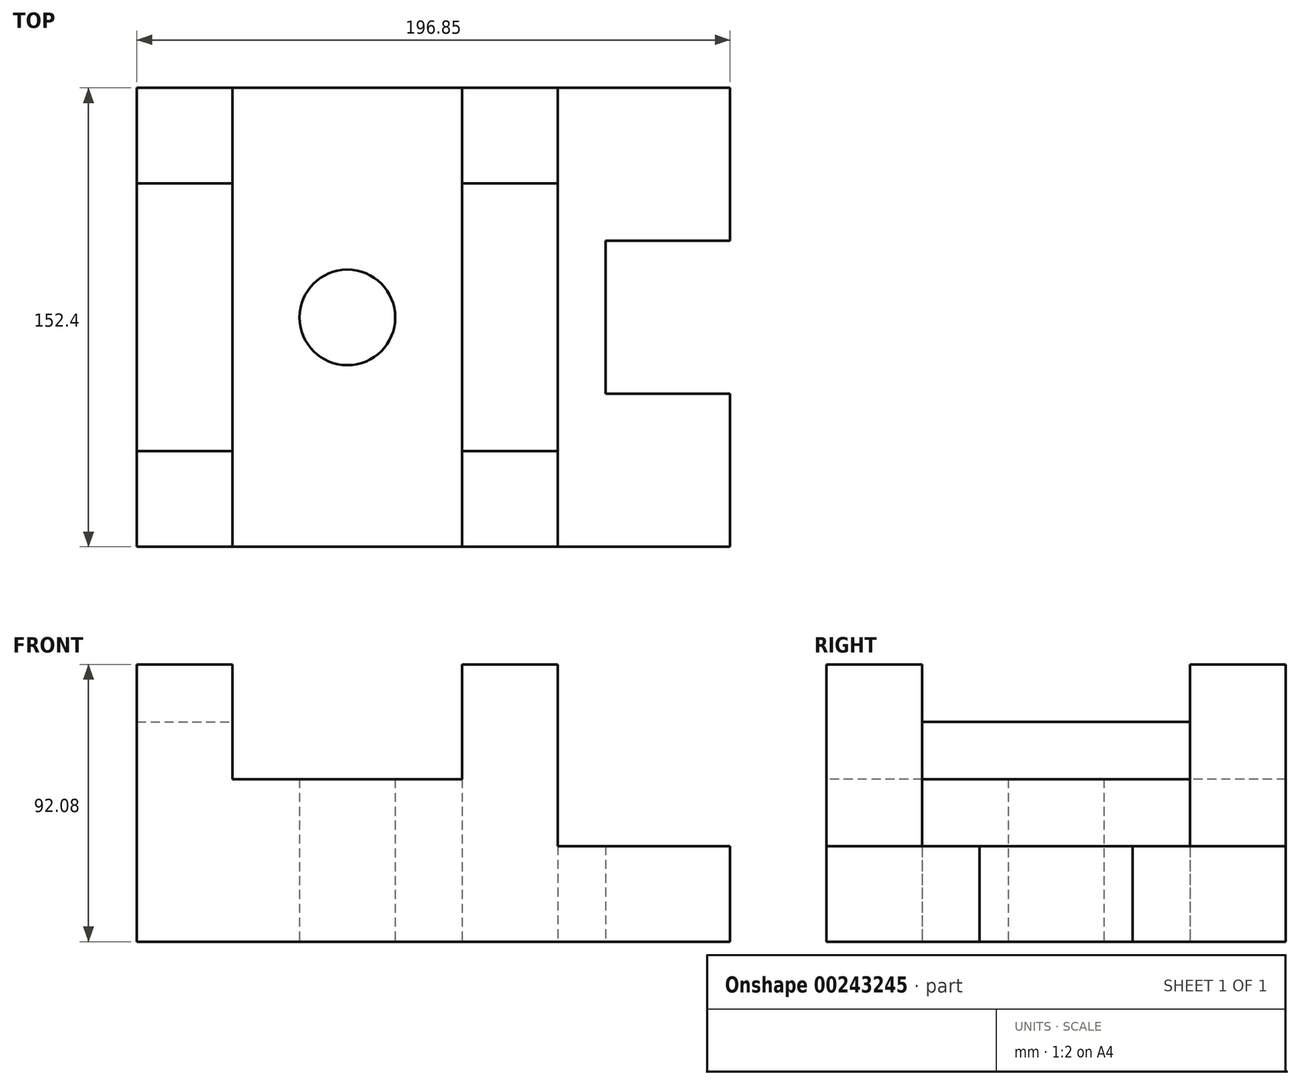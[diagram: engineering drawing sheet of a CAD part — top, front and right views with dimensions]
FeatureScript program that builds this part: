
annotation { "Feature Type Name" : "Feature", "Feature Type Description" : "" }
export const myFeature = defineFeature(function(context is Context, id is Id, definition is map)
    precondition{}
    {
        {
            var Q0;
            Q0=qCreatedBy(makeId("Top.planeOp"),FACE);
            var sketch = newSketch(context, id + "F0", { "sketchPlane" : qUnion([Q0])});
            skLineSegment(sketch, "E0.left", {"start": v(-114.8, 83.68) * mm, "end": v(-114.8, -68.72) * mm});
            skLineSegment(sketch, "E1.bottom", {"start": v(-114.8, 83.68) * mm, "end": v(-57.65, 83.68) * mm});
            skLineSegment(sketch, "E1.top", {"start": v(-114.8, -68.72) * mm, "end": v(-57.65, -68.72) * mm});
            skLineSegment(sketch, "E1.right", {"start": v(-57.65, 83.68) * mm, "end": v(-57.65, -68.72) * mm});
            skLineSegment(sketch, "E2.bottom", {"start": v(-57.65, 83.68) * mm, "end": v(-25.9, 83.68) * mm});
            skLineSegment(sketch, "E2.top", {"start": v(-57.65, -68.72) * mm, "end": v(-25.9, -68.72) * mm});
            skLineSegment(sketch, "E2.right", {"start": v(-25.9, 83.68) * mm, "end": v(-25.9, -68.72) * mm});
            skLineSegment(sketch, "E3.MirrorCS", {"start": v(-114.8, -68.72) * mm, "end": v(-114.8, 83.68) * mm});
            skLineSegment(sketch, "E4.MirrorCS", {"start": v(-57.65, -68.72) * mm, "end": v(-57.65, 83.68) * mm});
            skLineSegment(sketch, "E5.MirrorCS", {"start": v(-25.9, -68.72) * mm, "end": v(-25.9, 83.68) * mm});
            skPoint(sketch, "E6.endSnap0", {"position": v(50.3, -68.72) * mm});
            skLineSegment(sketch, "E7.MirrorCS", {"start": v(-57.65, -68.72) * mm, "end": v(-57.65, -36.97) * mm});
            skLineSegment(sketch, "E8.MirrorCS", {"start": v(-114.8, -17.92) * mm, "end": v(-114.8, 32.88) * mm});
            skLineSegment(sketch, "E9.MirrorCS", {"start": v(-114.8, -68.72) * mm, "end": v(-114.8, -17.92) * mm});
            skLineSegment(sketch, "E10.MirrorCS", {"start": v(-57.65, 83.68) * mm, "end": v(-57.65, 51.93) * mm});
            skLineSegment(sketch, "E11.MirrorCS", {"start": v(-114.8, 83.68) * mm, "end": v(-114.8, 32.88) * mm});
            skLineSegment(sketch, "E12.MirrorCS", {"start": v(-114.8, 32.88) * mm, "end": v(-73.52, 32.88) * mm});
            skLineSegment(sketch, "E13.MirrorCS", {"start": v(-114.8, 32.88) * mm, "end": v(-114.8, -17.92) * mm});
            skLineSegment(sketch, "E14.MirrorCS", {"start": v(-114.8, -17.92) * mm, "end": v(-73.52, -17.92) * mm});
            skLineSegment(sketch, "E15.MirrorCS", {"start": v(-73.52, -17.92) * mm, "end": v(-73.52, 32.88) * mm});
            skLineSegment(sketch, "E16.MirrorCS", {"start": v(-57.65, -36.97) * mm, "end": v(-25.9, -36.97) * mm});
            skLineSegment(sketch, "E17.MirrorCS", {"start": v(-25.9, 83.68) * mm, "end": v(-25.9, 51.93) * mm});
            skLineSegment(sketch, "E18.MirrorCS", {"start": v(-73.52, 32.88) * mm, "end": v(-73.52, -17.92) * mm});
            skLineSegment(sketch, "E19.MirrorCS", {"start": v(-57.65, 51.93) * mm, "end": v(-25.9, 51.93) * mm});
            skPoint(sketch, "E20.MirrorP", {"position": v(3.96, -68.72) * mm});
            skLineSegment(sketch, "E21.MirrorCS", {"start": v(-25.9, -68.72) * mm, "end": v(-25.9, -36.97) * mm});
            skLineSegment(sketch, "E22.bottom", {"start": v(-25.9, 83.68) * mm, "end": v(50.3, 83.68) * mm});
            skLineSegment(sketch, "E22.top", {"start": v(-25.9, -68.72) * mm, "end": v(50.3, -68.72) * mm});
            skLineSegment(sketch, "E22.right", {"start": v(50.3, 83.68) * mm, "end": v(50.3, -68.72) * mm});
            skPoint(sketch, "E23.endSnap0", {"position": v(50.3, 7.48) * mm});
            skLineSegment(sketch, "E24.bottom", {"start": v(50.3, 83.68) * mm, "end": v(82.05, 83.68) * mm});
            skLineSegment(sketch, "E24.top", {"start": v(50.3, 51.93) * mm, "end": v(82.05, 51.93) * mm});
            skLineSegment(sketch, "E24.left", {"start": v(50.3, 83.68) * mm, "end": v(50.3, 51.93) * mm});
            skLineSegment(sketch, "E24.right", {"start": v(82.05, 83.68) * mm, "end": v(82.05, 51.93) * mm});
            skLineSegment(sketch, "E25.bottom", {"start": v(50.3, -68.72) * mm, "end": v(82.05, -68.72) * mm});
            skLineSegment(sketch, "E25.top", {"start": v(50.3, -36.97) * mm, "end": v(82.05, -36.97) * mm});
            skLineSegment(sketch, "E25.left", {"start": v(50.3, -68.72) * mm, "end": v(50.3, -36.97) * mm});
            skLineSegment(sketch, "E25.right", {"start": v(82.05, -68.72) * mm, "end": v(82.05, -36.97) * mm});
            skLineSegment(sketch, "E26.bottom", {"start": v(82.05, 51.93) * mm, "end": v(50.3, 51.93) * mm});
            skLineSegment(sketch, "E26.top", {"start": v(82.05, -36.97) * mm, "end": v(50.3, -36.97) * mm});
            skLineSegment(sketch, "E26.left", {"start": v(82.05, 51.93) * mm, "end": v(82.05, -36.97) * mm});
            skLineSegment(sketch, "E26.right", {"start": v(50.3, 51.93) * mm, "end": v(50.3, -36.97) * mm});
            skLineSegment(sketch, "E27.bottom", {"start": v(82.05, 83.68) * mm, "end": v(139.2, 83.68) * mm});
            skLineSegment(sketch, "E27.top", {"start": v(82.05, -68.72) * mm, "end": v(139.2, -68.72) * mm});
            skLineSegment(sketch, "E27.left", {"start": v(82.05, 83.68) * mm, "end": v(82.05, -68.72) * mm});
            skLineSegment(sketch, "E27.right", {"start": v(139.2, 83.68) * mm, "end": v(139.2, -68.72) * mm});
            skLineSegment(sketch, "E28", {"start": v(139.2, -68.72) * mm, "end": v(139.2, -17.92) * mm});
            skLineSegment(sketch, "E29.bottom", {"start": v(139.2, -17.92) * mm, "end": v(97.93, -17.92) * mm});
            skLineSegment(sketch, "E29.top", {"start": v(139.2, 32.88) * mm, "end": v(97.93, 32.88) * mm});
            skLineSegment(sketch, "E29.left", {"start": v(139.2, -17.92) * mm, "end": v(139.2, 32.88) * mm});
            skLineSegment(sketch, "E29.right", {"start": v(97.93, -17.92) * mm, "end": v(97.93, 32.88) * mm});
            skCircle(sketch, "E30", {"center": v(12.2, 7.48) * mm, "radius": 15.88 * mm});
            skSolve(sketch);
        }
        {
            var Q0;
            {var subQ3=sQuery(id+"F0.wireOp",EDGE,"E14.MirrorCS");Q0=makeQuery(id+"F0.imprint","IMPRINT",FACE,{"disambiguationData":[TD([[makeQuery(id+"F0.imprint","IMPRINT",EDGE,{"derivedFrom":subQ3}),-1.0]])]});}
            var Q1;
            {var subQ8=sQuery(id+"F0.wireOp",EDGE,"bafb01ee-b0b1-46f3-aeee-ee639ae67d908.MirrorCS");Q1=makeQuery(id+"F0.imprint","IMPRINT",FACE,{"disambiguationData":[TD([[makeQuery(id+"F0.imprint","IMPRINT",EDGE,{"derivedFrom":subQ8}),1.0]])]});}
            var Q2;
            Q2=makeQuery(id+"F0.imprint","IMPRINT",FACE,{"disambiguationData":[TD([[makeQuery(id+"F0.imprint","IMPRINT",EDGE,{"derivedFrom":sQuery(id+"F0.wireOp",EDGE,"OqLtfph7-jQ8x-I92G-y3ap-m9EuBUkJHxD9")}),1.0]])]});
            var Q3;
            {var subQ3=sQuery(id+"F0.wireOp",EDGE,"E27.bottom");Q3=makeQuery(id+"F0.imprint","IMPRINT",FACE,{"disambiguationData":[TD([[makeQuery(id+"F0.imprint","IMPRINT",EDGE,{"derivedFrom":subQ3}),-1.0]])]});}
            extrude(context, id + "F1", {"entities" : qUnion([Q0, Q1, Q2, Q3]), "depth" : 31.75 * mm});
        }
        {
            var Q0;
            {var subQ3=sQuery(id+"F0.wireOp",EDGE,"E22.bottom");Q0=makeQuery(id+"F0.imprint","IMPRINT",FACE,{"disambiguationData":[TD([[makeQuery(id+"F0.imprint","IMPRINT",EDGE,{"derivedFrom":subQ3}),-1.0]])]});}
            extrude(context, id + "F2", {"entities" : qUnion([Q0]), "depth" : 53.97 * mm});
        }
        {
            var Q0;
            {var subQ0=sQuery(id+"F0.wireOp",EDGE,"E16.MirrorCS");Q0=makeQuery(id+"F0.imprint","IMPRINT",FACE,{"disambiguationData":[TD([[makeQuery(id+"F0.imprint","IMPRINT",EDGE,{"derivedFrom":subQ0}),-1.0]])]});}
            var Q1;
            Q1=makeQuery(id+"F0.imprint","IMPRINT",FACE,{"disambiguationData":[TD([[makeQuery(id+"F0.imprint","IMPRINT",EDGE,{"derivedFrom":sQuery(id+"F0.wireOp",EDGE,"E17.MirrorCS")}),-1.0]])]});
            var Q2;
            {var subQ0=sQuery(id+"F0.wireOp",EDGE,"bafb01ee-b0b1-46f3-aeee-ee639ae67d9011.MirrorCS");Q2=makeQuery(id+"F0.imprint","IMPRINT",FACE,{"disambiguationData":[TD([[makeQuery(id+"F0.imprint","IMPRINT",EDGE,{"derivedFrom":subQ0}),-1.0]])]});}
            var Q3;
            {var subQ0=sQuery(id+"F0.wireOp",EDGE,"pMscXdNz-vYXx-GYS9-83aA-HiP6jFsDXhJ5.top");Q3=makeQuery(id+"F0.imprint","IMPRINT",FACE,{"disambiguationData":[TD([[makeQuery(id+"F0.imprint","IMPRINT",EDGE,{"derivedFrom":subQ0}),1.0]])]});}
            var Q4;
            {var subQ2=sQuery(id+"F0.wireOp",EDGE,"E19.MirrorCS");Q4=makeQuery(id+"F0.imprint","IMPRINT",FACE,{"disambiguationData":[TD([[makeQuery(id+"F0.imprint","IMPRINT",EDGE,{"derivedFrom":subQ2}),1.0]])]});}
            var Q5;
            {var subQ0=sQuery(id+"F0.wireOp",EDGE,"E24.bottom");Q5=makeQuery(id+"F0.imprint","IMPRINT",FACE,{"disambiguationData":[TD([[makeQuery(id+"F0.imprint","IMPRINT",EDGE,{"derivedFrom":subQ0}),-1.0]])]});}
            var Q6;
            {var subQ0=sQuery(id+"F0.wireOp",EDGE,"E25.bottom");Q6=makeQuery(id+"F0.imprint","IMPRINT",FACE,{"disambiguationData":[TD([[makeQuery(id+"F0.imprint","IMPRINT",EDGE,{"derivedFrom":subQ0}),1.0]])]});}
            extrude(context, id + "F3", {"entities" : qUnion([Q0, Q1, Q2, Q3, Q4, Q5, Q6]), "operationType" : NewBodyOperationType.ADD, "depth" : 92.07 * mm});
        }
        {
            var Q0;
            {var subQ0=sQuery(id+"F0.wireOp",EDGE,"pMscXdNz-vYXx-GYS9-83aA-HiP6jFsDXhJ5.top");Q0=makeQuery(id+"F0.imprint","IMPRINT",FACE,{"disambiguationData":[TD([[makeQuery(id+"F0.imprint","IMPRINT",EDGE,{"derivedFrom":subQ0}),-1.0]])]});}
            var Q1;
            {var subQ0=sQuery(id+"F0.wireOp",EDGE,"E16.MirrorCS");Q1=makeQuery(id+"F0.imprint","IMPRINT",FACE,{"disambiguationData":[TD([[makeQuery(id+"F0.imprint","IMPRINT",EDGE,{"derivedFrom":subQ0}),1.0]])]});}
            var Q2;
            {var subQ0=sQuery(id+"F0.wireOp",EDGE,"E26.bottom");Q2=makeQuery(id+"F0.imprint","IMPRINT",FACE,{"disambiguationData":[TD([[makeQuery(id+"F0.imprint","IMPRINT",EDGE,{"derivedFrom":subQ0}),1.0]])]});}
            extrude(context, id + "F4", {"entities" : qUnion([Q0, Q1, Q2]), "operationType" : NewBodyOperationType.ADD, "depth" : 73.02 * mm});
        }
    });
